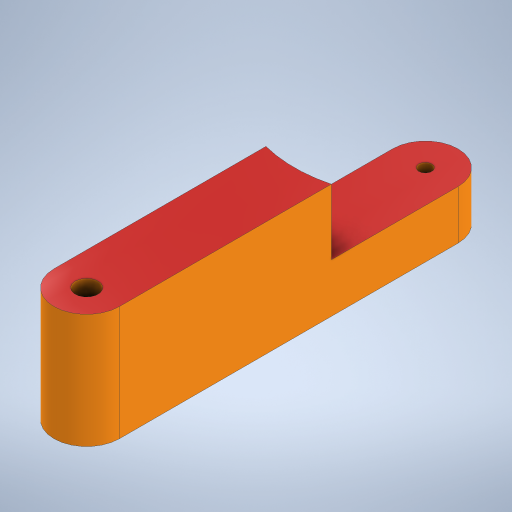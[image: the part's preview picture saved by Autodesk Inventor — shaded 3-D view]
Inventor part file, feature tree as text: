
AUTODESK INVENTOR PART (.ipt)
format: ipt  version: 2023 (Build 270158000, 158)  size: 273,920 bytes
history: native  units: mm
features: extrude x2, sketch x1
ambient origin geometry x8: Origin, YZ Plane, XZ Plane, XY Plane, X Axis, Y Axis, Z Axis, Center Point
bodies: Solid1 (feature_tree)
feature tree (3):
  sketch  "Sketch1"  dims[d1=120.0mm d2=200.0mm d3=15.0deg d4=10.0mm d5=10.0mm d6=80.0mm d7=360.0deg d8=7.0mm d9=4.0mm d10=20.0mm d11=20.0mm d12=20.0mm d13=0.0mm d14=15.0mm d15=0.0mm]
  extrude  "Extrusion1"  Depth=20.0mm
  extrude  "Extrusion2"  Depth=20.0mm
